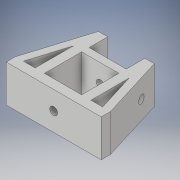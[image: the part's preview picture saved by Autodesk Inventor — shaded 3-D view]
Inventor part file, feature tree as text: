
AUTODESK INVENTOR PART (.ipt)
format: ipt  version: 2018 (Build 220112000, 112)  size: 154,624 bytes
history: native  units: in
note: dims shown in document units (in); Inventor stores cm internally (conversion verified against a paired STEP export)
features: extrude x5, sketch x5
ambient origin geometry x8: Origin, YZ Plane, XZ Plane, XY Plane, X Axis, Y Axis, Z Axis, Center Point
bodies: Solid1 (feature_tree)
feature tree (10):
  extrude  "Extrusion1"  Depth=0.7874in
  extrude  "Extrusion2"  Depth=0.7874in
  extrude  "Extrusion3"  Depth=0.1969in
  extrude  "Extrusion4"  Depth=0.1575in
  extrude  "Extrusion5"  Depth=0.1969in TaperAngle=0.0deg
  sketch  "Sketch1"  dims[d0=2.0079in d1=0.7874in]
  sketch  "Sketch2"  dims[d2=0.1969in d3=0.0in d4=0.7874in]
  sketch  "Sketch3"  dims[d5=0.1969in d6=0.1969in]
  sketch  "Sketch4"  dims[d7=1.3386in d8=0.1575in]
  sketch  "Sketch5"  dims[d9=0.1575in d10=0.1969in d11=0.0in d12=0.1654in d13=0.3937in d14=1.5748in d15=0.0in d16=1.5748in d17=0.0in d18=0.3937in d19=0.1575in d20=0.1969in d21=0.0in d22=0.1654in d23=0.1969in d24=0.0in]
